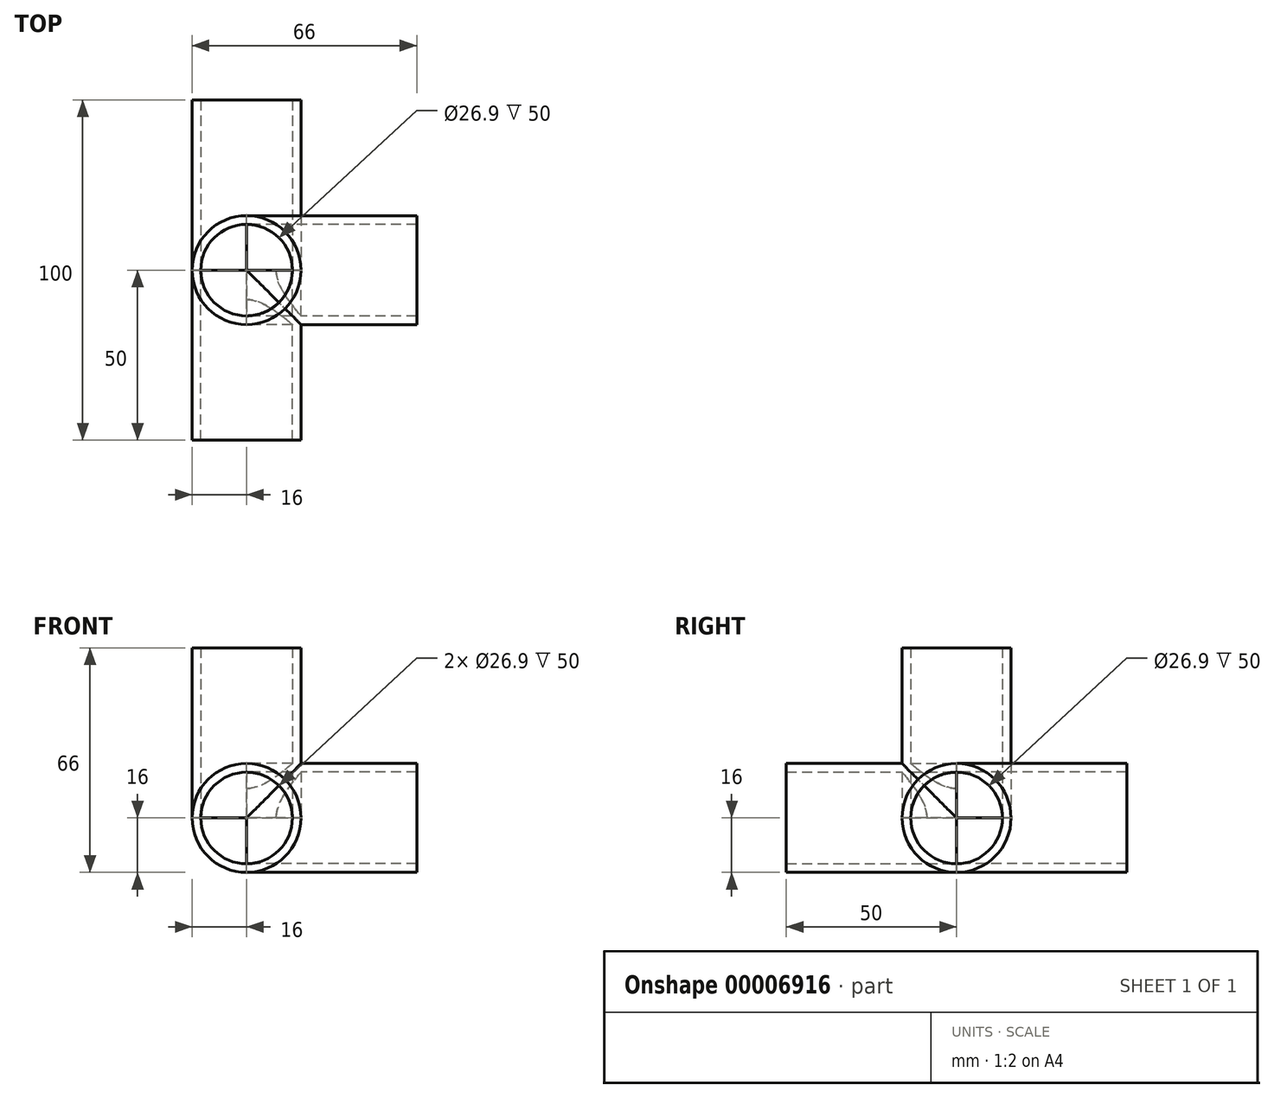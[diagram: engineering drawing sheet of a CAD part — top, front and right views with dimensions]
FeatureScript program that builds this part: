
annotation { "Feature Type Name" : "Feature", "Feature Type Description" : "" }
export const myFeature = defineFeature(function(context is Context, id is Id, definition is map)
    precondition{}
    {
        {
            var Q0;
            Q0=qCreatedBy(makeId("Top.planeOp"),FACE);
            var sketch = newSketch(context, id + "F0", { "sketchPlane" : qUnion([Q0])});
            skCircle(sketch, "E0", {"center": v(0, 0) * mm, "radius": 13.45 * mm});
            skCircle(sketch, "E1", {"center": v(0, 0) * mm, "radius": 16 * mm});
            skSolve(sketch);
        }
        {
            var Q0;
            Q0=makeQuery(id+"F0.imprint","IMPRINT",FACE,{"disambiguationData":[TD([[makeQuery(id+"F0.imprint","IMPRINT",EDGE,{"derivedFrom":sQuery(id+"F0.wireOp",EDGE,"E0")}),-1.0]])]});
            extrude(context, id + "F1", {"entities" : qUnion([Q0]), "depth" : 50 * mm});
        }
        {
            var Q0;
            Q0=qCreatedBy(makeId("Front.planeOp"),FACE);
            var sketch = newSketch(context, id + "F2", { "sketchPlane" : qUnion([Q0])});
            skCircle(sketch, "E2", {"center": v(0, 0) * mm, "radius": 16 * mm});
            skCircle(sketch, "E3", {"center": v(0, 0) * mm, "radius": 13.45 * mm});
            skSolve(sketch);
        }
        {
            var Q0;
            Q0=makeQuery(id+"F2.imprint","IMPRINT",FACE,{"disambiguationData":[TD([[makeQuery(id+"F2.imprint","IMPRINT",EDGE,{"derivedFrom":sQuery(id+"F2.wireOp",EDGE,"E2")}),1.0]])]});
            extrude(context, id + "F3", {"entities" : qUnion([Q0]), "operationType" : NewBodyOperationType.ADD, "depth" : 50 * mm});
        }
        {
            var Q0;
            Q0=qCreatedBy(makeId("Right.planeOp"),FACE);
            var sketch = newSketch(context, id + "F4", { "sketchPlane" : qUnion([Q0])});
            skCircle(sketch, "E4", {"center": v(0, 0) * mm, "radius": 13.45 * mm});
            skCircle(sketch, "E5", {"center": v(0, 0) * mm, "radius": 16 * mm});
            skSolve(sketch);
        }
        {
            var Q0;
            Q0=qSketchRegion(id+"F4",true);
            extrude(context, id + "F5", {"entities" : qUnion([Q0]), "operationType" : NewBodyOperationType.ADD, "depth" : 50 * mm});
        }
        {
            var Q0;
            Q0=makeQuery(id+"F2.imprint","IMPRINT",FACE,{"disambiguationData":[TD([[makeQuery(id+"F2.imprint","IMPRINT",EDGE,{"derivedFrom":sQuery(id+"F2.wireOp",EDGE,"E2")}),1.0]])]});
            var Q1;
            Q1=sQuery(id+"F2.wireOp",EDGE,"E2");
            var Q2;
            Q2=sQuery(id+"F2.wireOp",EDGE,"E3");
            extrude(context, id + "F6", {"entities" : qUnion([Q0]), "surfaceEntities" : qUnion([Q1, Q2]), "oppositeDirection" : true, "depth" : 50 * mm});
        }
    });
